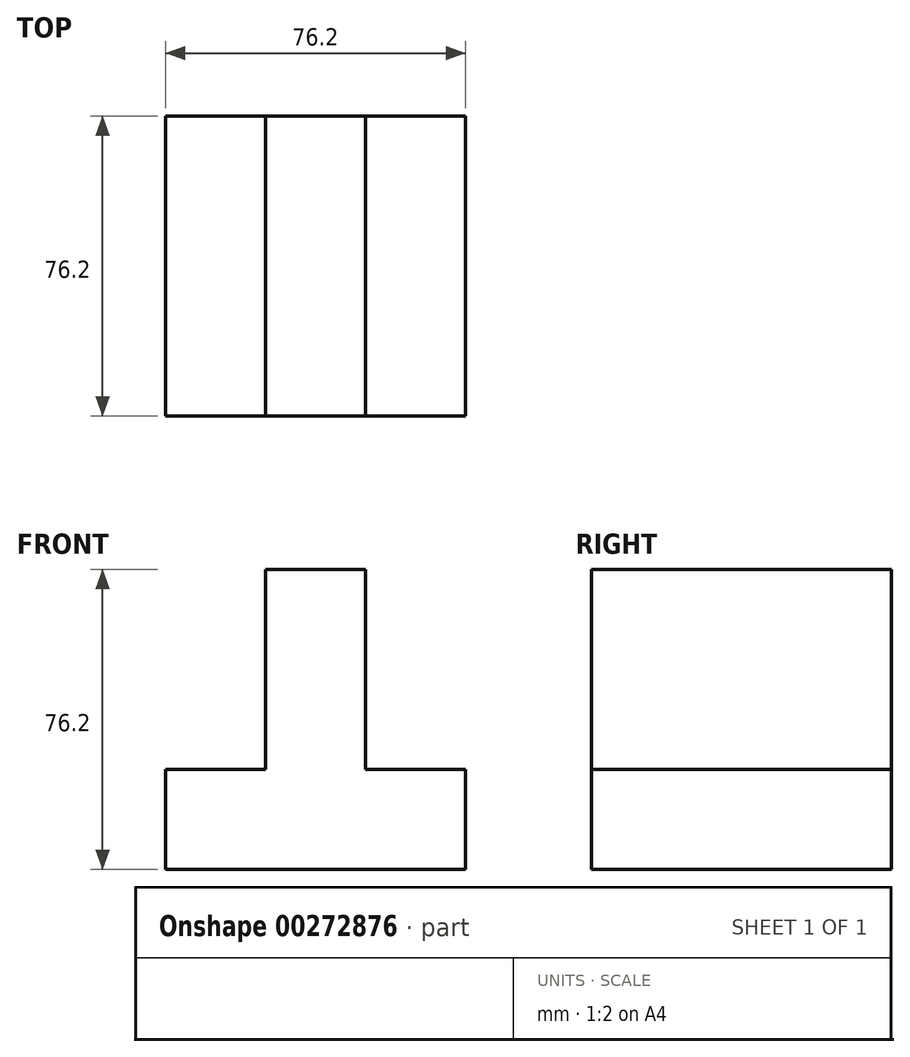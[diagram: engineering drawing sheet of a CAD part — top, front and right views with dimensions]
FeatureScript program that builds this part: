
annotation { "Feature Type Name" : "Feature", "Feature Type Description" : "" }
export const myFeature = defineFeature(function(context is Context, id is Id, definition is map)
    precondition{}
    {
        {
            var Q0;
            Q0=qCreatedBy(makeId("Front.planeOp"),FACE);
            var sketch = newSketch(context, id + "F0", { "sketchPlane" : qUnion([Q0])});
            skLineSegment(sketch, "E0", {"start": v(0, 0) * mm, "end": v(-76.2, 0) * mm});
            skLineSegment(sketch, "E1", {"start": v(-76.2, 0) * mm, "end": v(-76.2, 25.4) * mm});
            skLineSegment(sketch, "E2", {"start": v(-76.2, 25.4) * mm, "end": v(-50.8, 25.4) * mm});
            skLineSegment(sketch, "E3", {"start": v(-50.8, 25.4) * mm, "end": v(-50.8, 50.8) * mm});
            skLineSegment(sketch, "E4", {"start": v(-50.8, 50.8) * mm, "end": v(-50.8, 76.2) * mm});
            skLineSegment(sketch, "E5", {"start": v(-50.8, 76.2) * mm, "end": v(-25.4, 76.2) * mm});
            skLineSegment(sketch, "E6", {"start": v(-25.4, 76.2) * mm, "end": v(-25.4, 25.4) * mm});
            skLineSegment(sketch, "E7", {"start": v(-25.4, 25.4) * mm, "end": v(0, 25.4) * mm});
            skLineSegment(sketch, "E8", {"start": v(0, 25.4) * mm, "end": v(0, 0) * mm});
            skSolve(sketch);
        }
        {
            var Q0;
            Q0 = qSketchRegion(id + "F0", true);
            extrude(context, id + "F1", {"entities" : qUnion([Q0]), "depth" : 76.2 * mm});
        }
    });
